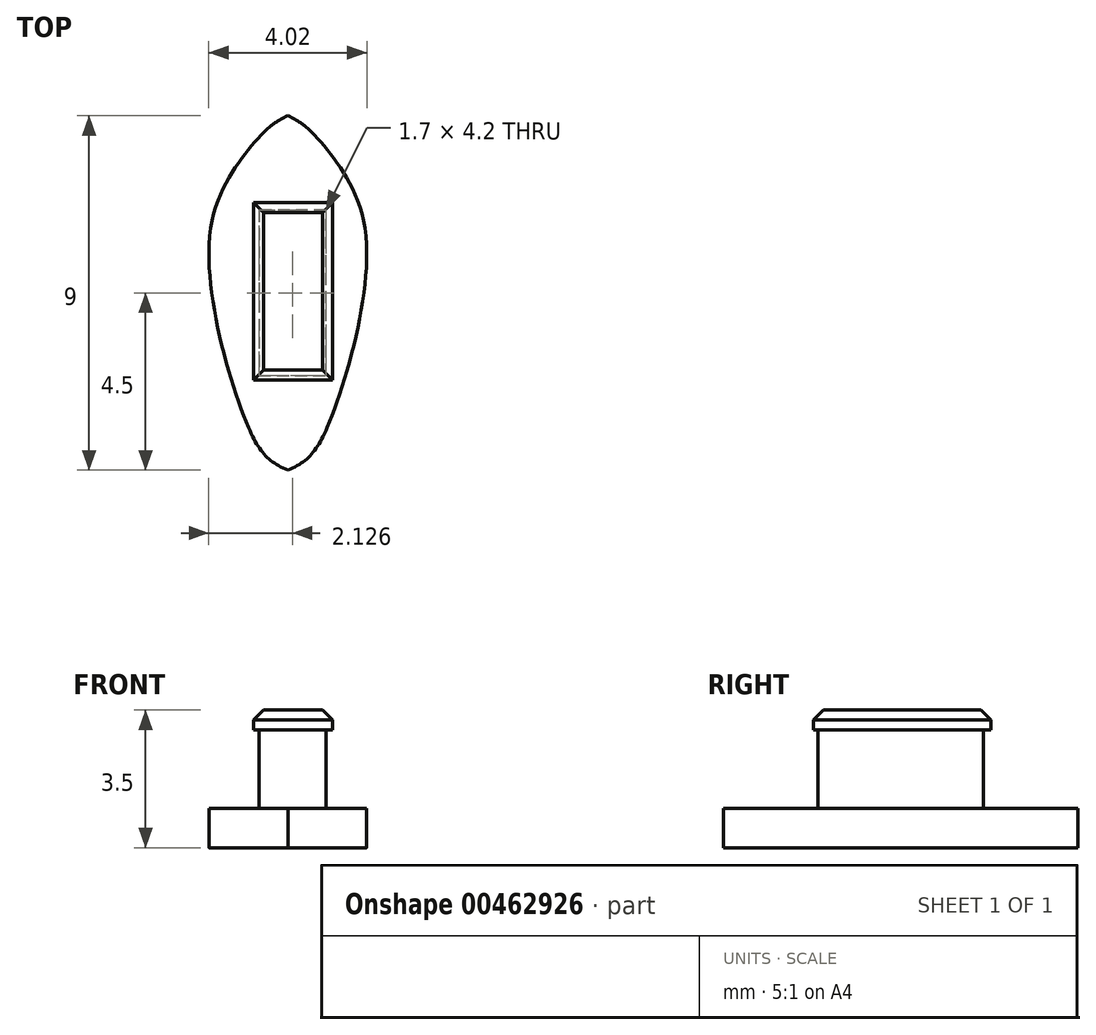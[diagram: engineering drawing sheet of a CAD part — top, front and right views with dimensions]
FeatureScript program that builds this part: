
annotation { "Feature Type Name" : "Feature", "Feature Type Description" : "" }
export const myFeature = defineFeature(function(context is Context, id is Id, definition is map)
    precondition{}
    {
        {
            var Q0;
            Q0=qCreatedBy(makeId("Top.planeOp"),FACE);
            var sketch = newSketch(context, id + "F0", { "sketchPlane" : qUnion([Q0])});
            skFitSpline(sketch, "E0", {"points": [v(0, 9) * mm, v(-0.45, 8.73) * mm, v(-1.23, 7.84) * mm, v(-2, 5.73) * mm, v(-1, 1.08) * mm, v(0, 0) * mm], "startDerivative": vector(-4.17, -1.94) * mm, "endDerivative": vector(8.3, -3.13) * mm});
            skLineSegment(sketch, "E1", {"start": v(0, 9) * mm, "end": v(0, 0) * mm});
            skFitSpline(sketch, "E2.MirrorCS", {"points": [v(0, 9) * mm, v(0.45, 8.73) * mm, v(1.23, 7.84) * mm, v(2, 5.73) * mm, v(1, 1.08) * mm, v(0, 0) * mm], "startDerivative": vector(4.17, -1.94) * mm, "endDerivative": vector(-8.3, -3.13) * mm});
            skLineSegment(sketch, "E3", {"start": v(-2, 5.73) * mm, "end": v(2, 5.73) * mm});
            skLineSegment(sketch, "E4", {"start": v(-1, 1.08) * mm, "end": v(1, 1.08) * mm});
            skLineSegment(sketch, "E5", {"start": v(-0.45, 8.73) * mm, "end": v(0.45, 8.73) * mm});
            skSolve(sketch);
        }
        {
            var Q0;
            {var subQ0=sQuery(id+"F0.wireOp",EDGE,"E3");var subQ1=sQuery(id+"F0.wireOp",EDGE,"E0");var subQ2=makeQuery(id+"F0.imprint","INTERSECT",VERTEX,{"derivedFrom":[subQ1,subQ0]});Q0=makeQuery(id+"F0.imprint","IMPRINT",FACE,{"disambiguationData":[TD([[makeQuery(id+"F0.imprint","IMPRINT",EDGE,{"disambiguationData":[TD([[subQ2,-1.0]])],"derivedFrom":subQ1}),1.0]])]});}
            var Q1;
            {var subQ0=sQuery(id+"F0.wireOp",EDGE,"E3");var subQ1=sQuery(id+"F0.wireOp",EDGE,"E0");var subQ2=makeQuery(id+"F0.imprint","INTERSECT",VERTEX,{"derivedFrom":[subQ1,subQ0]});Q1=makeQuery(id+"F0.imprint","IMPRINT",FACE,{"disambiguationData":[TD([[makeQuery(id+"F0.imprint","IMPRINT",EDGE,{"disambiguationData":[TD([[subQ2,1.0]])],"derivedFrom":subQ1}),1.0]])]});}
            var Q2;
            {var subQ0=sQuery(id+"F0.wireOp",EDGE,"E5");var subQ1=sQuery(id+"F0.wireOp",EDGE,"E1");var subQ2=makeQuery(id+"F0.imprint","INTERSECT",VERTEX,{"derivedFrom":[subQ1,subQ0]});Q2=makeQuery(id+"F0.imprint","IMPRINT",FACE,{"disambiguationData":[TD([[makeQuery(id+"F0.imprint","IMPRINT",EDGE,{"disambiguationData":[TD([[subQ2,-1.0]])],"derivedFrom":subQ1}),1.0]])]});}
            var Q3;
            {var subQ0=sQuery(id+"F0.wireOp",EDGE,"E3");var subQ1=sQuery(id+"F0.wireOp",EDGE,"E1");var subQ2=makeQuery(id+"F0.imprint","INTERSECT",VERTEX,{"derivedFrom":[subQ1,subQ0]});Q3=makeQuery(id+"F0.imprint","IMPRINT",FACE,{"disambiguationData":[TD([[makeQuery(id+"F0.imprint","IMPRINT",EDGE,{"disambiguationData":[TD([[subQ2,-1.0]])],"derivedFrom":subQ1}),1.0]])]});}
            var Q4;
            {var subQ0=sQuery(id+"F0.wireOp",EDGE,"E2.MirrorCS");var subQ3=sQuery(id+"F0.wireOp",EDGE,"E4");var subQ5=makeQuery(id+"F0.imprint","INTERSECT",VERTEX,{"derivedFrom":[subQ0,subQ3]});Q4=makeQuery(id+"F0.imprint","IMPRINT",FACE,{"disambiguationData":[TD([[makeQuery(id+"F0.imprint","IMPRINT",EDGE,{"disambiguationData":[TD([[subQ5,1.0]])],"derivedFrom":subQ3}),-1.0]])]});}
            var Q5;
            {var subQ1=sQuery(id+"F0.wireOp",EDGE,"E0");var subQ3=sQuery(id+"F0.wireOp",EDGE,"E4");var subQ4=makeQuery(id+"F0.imprint","INTERSECT",VERTEX,{"derivedFrom":[subQ1,subQ3]});Q5=makeQuery(id+"F0.imprint","IMPRINT",FACE,{"disambiguationData":[TD([[makeQuery(id+"F0.imprint","IMPRINT",EDGE,{"disambiguationData":[TD([[subQ4,-1.0]])],"derivedFrom":subQ3}),-1.0]])]});}
            var Q6;
            {var subQ0=sQuery(id+"F0.wireOp",EDGE,"E2.MirrorCS");var subQ3=sQuery(id+"F0.wireOp",EDGE,"E5");var subQ5=makeQuery(id+"F0.imprint","INTERSECT",VERTEX,{"derivedFrom":[subQ0,subQ3]});Q6=makeQuery(id+"F0.imprint","IMPRINT",FACE,{"disambiguationData":[TD([[makeQuery(id+"F0.imprint","IMPRINT",EDGE,{"disambiguationData":[TD([[subQ5,1.0]])],"derivedFrom":subQ3}),1.0]])]});}
            var Q7;
            {var subQ1=sQuery(id+"F0.wireOp",EDGE,"E0");var subQ3=sQuery(id+"F0.wireOp",EDGE,"E5");var subQ4=makeQuery(id+"F0.imprint","INTERSECT",VERTEX,{"derivedFrom":[subQ1,subQ3]});Q7=makeQuery(id+"F0.imprint","IMPRINT",FACE,{"disambiguationData":[TD([[makeQuery(id+"F0.imprint","IMPRINT",EDGE,{"disambiguationData":[TD([[subQ4,-1.0]])],"derivedFrom":subQ3}),1.0]])]});}
            extrude(context, id + "F1", {"entities" : qUnion([Q0, Q1, Q2, Q3, Q4, Q5, Q6, Q7]), "depth" : 1 * mm});
        }
        {
            var Q0;
            Q0=makeQuery(id+"F1.opExtrude","CAP_FACE",FACE,{"disambiguationData":[OSD([sQuery(id+"F0.wireOp",EDGE,"E0"),sQuery(id+"F0.wireOp",EDGE,"E2.MirrorCS")])],"isStart":false});
            var sketch = newSketch(context, id + "F2", { "sketchPlane" : qUnion([Q0])});
            skLineSegment(sketch, "E6", {"start": v(0, 0) * mm, "end": v(0, 4.5) * mm});
            skLineSegment(sketch, "E7", {"start": v(0, 4.5) * mm, "end": v(1.93, 4.5) * mm});
            skLineSegment(sketch, "E8", {"start": v(0.97, 4.5) * mm, "end": v(0.97, 6.6) * mm});
            skLineSegment(sketch, "E9", {"start": v(0.97, 4.5) * mm, "end": v(0.97, 2.4) * mm});
            skLineSegment(sketch, "E10", {"start": v(0.97, 6.6) * mm, "end": v(-0.73, 6.6) * mm});
            skLineSegment(sketch, "E11", {"start": v(-0.73, 6.6) * mm, "end": v(-0.73, 2.4) * mm});
            skLineSegment(sketch, "E12", {"start": v(-0.73, 2.4) * mm, "end": v(0.97, 2.4) * mm});
            skSolve(sketch);
        }
        {
            var Q0;
            {var subQ0=sQuery(id+"F2.wireOp",EDGE,"E8");Q0=makeQuery(id+"F2.imprint","IMPRINT",FACE,{"disambiguationData":[TD([[makeQuery(id+"F2.imprint","IMPRINT",EDGE,{"derivedFrom":subQ0}),1.0]])]});}
            var Q1;
            {var subQ5=sQuery(id+"F2.wireOp",EDGE,"E9");Q1=makeQuery(id+"F2.imprint","IMPRINT",FACE,{"disambiguationData":[TD([[makeQuery(id+"F2.imprint","IMPRINT",EDGE,{"derivedFrom":subQ5}),-1.0]])]});}
            extrude(context, id + "F3", {"entities" : qUnion([Q0, Q1]), "operationType" : NewBodyOperationType.ADD, "depth" : 2 * mm});
        }
        {
            var Q0;
            Q0=makeQuery(id+"F3.opExtrude","CAP_FACE",FACE,{"disambiguationData":[OSD([sQuery(id+"F2.wireOp",EDGE,"E8"),sQuery(id+"F2.wireOp",EDGE,"E9"),sQuery(id+"F2.wireOp",EDGE,"E10"),sQuery(id+"F2.wireOp",EDGE,"E11"),sQuery(id+"F2.wireOp",EDGE,"E12")])],"isStart":false});
            var sketch = newSketch(context, id + "F4", { "sketchPlane" : qUnion([Q0])});
            skLineSegment(sketch, "E13", {"start": v(0.12, 6.79) * mm, "end": v(0.12, 2.29) * mm});
            skPoint(sketch, "E14", {"position": v(0.12, 6.6) * mm});
            skLineSegment(sketch, "E15", {"start": v(-0.87, 6.79) * mm, "end": v(1.13, 6.79) * mm});
            skLineSegment(sketch, "E16", {"start": v(-0.87, 2.29) * mm, "end": v(1.13, 2.29) * mm});
            skLineSegment(sketch, "E17", {"start": v(-0.87, 2.29) * mm, "end": v(-0.87, 6.79) * mm});
            skLineSegment(sketch, "E18", {"start": v(1.13, 6.79) * mm, "end": v(1.13, 2.29) * mm});
            skSolve(sketch);
        }
        {
            var Q0;
            {var subQ3=sQuery(id+"F4.wireOp",EDGE,"E17");Q0=makeQuery(id+"F4.imprint","IMPRINT",FACE,{"disambiguationData":[TD([[makeQuery(id+"F4.imprint","IMPRINT",EDGE,{"derivedFrom":subQ3}),-1.0]])]});}
            var Q1;
            {var subQ5=makeQuery(id+"F3.opExtrude","CAP_EDGE",EDGE,{"disambiguationData":[OSD([sQuery(id+"F2.wireOp",EDGE,"E11")])],"isStart":false});Q1=makeQuery(id+"F4.imprint","IMPRINT",FACE,{"disambiguationData":[TD([[makeQuery(id+"F4.imprint","IMPRINT",EDGE,{"derivedFrom":subQ5}),1.0]])]});}
            var Q2;
            {var subQ5=makeQuery(id+"F3.opExtrude","CAP_EDGE",EDGE,{"disambiguationData":[OSD([sQuery(id+"F2.wireOp",EDGE,"E8"),sQuery(id+"F2.wireOp",EDGE,"E9")])],"isStart":false});Q2=makeQuery(id+"F4.imprint","IMPRINT",FACE,{"disambiguationData":[TD([[makeQuery(id+"F4.imprint","IMPRINT",EDGE,{"derivedFrom":subQ5}),1.0]])]});}
            var Q3;
            {var subQ3=sQuery(id+"F4.wireOp",EDGE,"E18");Q3=makeQuery(id+"F4.imprint","IMPRINT",FACE,{"disambiguationData":[TD([[makeQuery(id+"F4.imprint","IMPRINT",EDGE,{"derivedFrom":subQ3}),-1.0]])]});}
            extrude(context, id + "F5", {"entities" : qUnion([Q0, Q1, Q2, Q3]), "operationType" : NewBodyOperationType.ADD, "depth" : .5 * mm});
        }
        {
            var Q0;
            Q0=makeQuery(id+"F5.opExtrude","CAP_EDGE",EDGE,{"disambiguationData":[OSD([sQuery(id+"F4.wireOp",EDGE,"E16")])],"isStart":false});
            var Q1;
            Q1=makeQuery(id+"F5.opExtrude","CAP_EDGE",EDGE,{"disambiguationData":[OSD([sQuery(id+"F4.wireOp",EDGE,"E18")])],"isStart":false});
            var Q2;
            Q2=makeQuery(id+"F5.opExtrude","CAP_EDGE",EDGE,{"disambiguationData":[OSD([sQuery(id+"F4.wireOp",EDGE,"E15")])],"isStart":false});
            var Q3;
            Q3=makeQuery(id+"F5.opExtrude","CAP_EDGE",EDGE,{"disambiguationData":[OSD([sQuery(id+"F4.wireOp",EDGE,"E17")])],"isStart":false});
            chamfer(context, id + "F6", {"entities" : qUnion([Q0, Q1, Q2, Q3]), "width" : .25 * mm, "tangentPropagation" : true});
        }
    });
